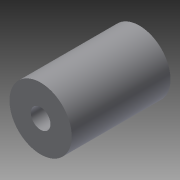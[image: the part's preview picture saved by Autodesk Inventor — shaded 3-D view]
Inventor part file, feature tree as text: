
AUTODESK INVENTOR PART (.ipt)
format: ipt  version: 2015 (Build 190159000, 159)  size: 93,184 bytes
history: native  units: mm
features: extrude x3, sketch x3
ambient origin geometry x8: Origin, YZ Plane, XZ Plane, XY Plane, X Axis, Y Axis, Z Axis, Center Point
bodies: Solid1 (feature_tree)
feature tree (6):
  extrude  "Extrusion1"  Depth=25.4mm TaperAngle=0.0deg
  extrude  "Extrusion2"  Depth=3.22mm
  extrude  "Extrusion3"  Depth=12.7mm TaperAngle=0.0deg
  sketch  "Sketch1"  dims[d0=16.0mm d1=25.4mm d2=0.0mm]
  sketch  "Sketch3"  dims[d13=3.22mm d15=1.61mm]
  sketch  "Sketch4"  dims[d16=1.61mm d17=12.7mm d18=0.0mm d19=5.05mm d20=12.7mm d21=0.0mm]
